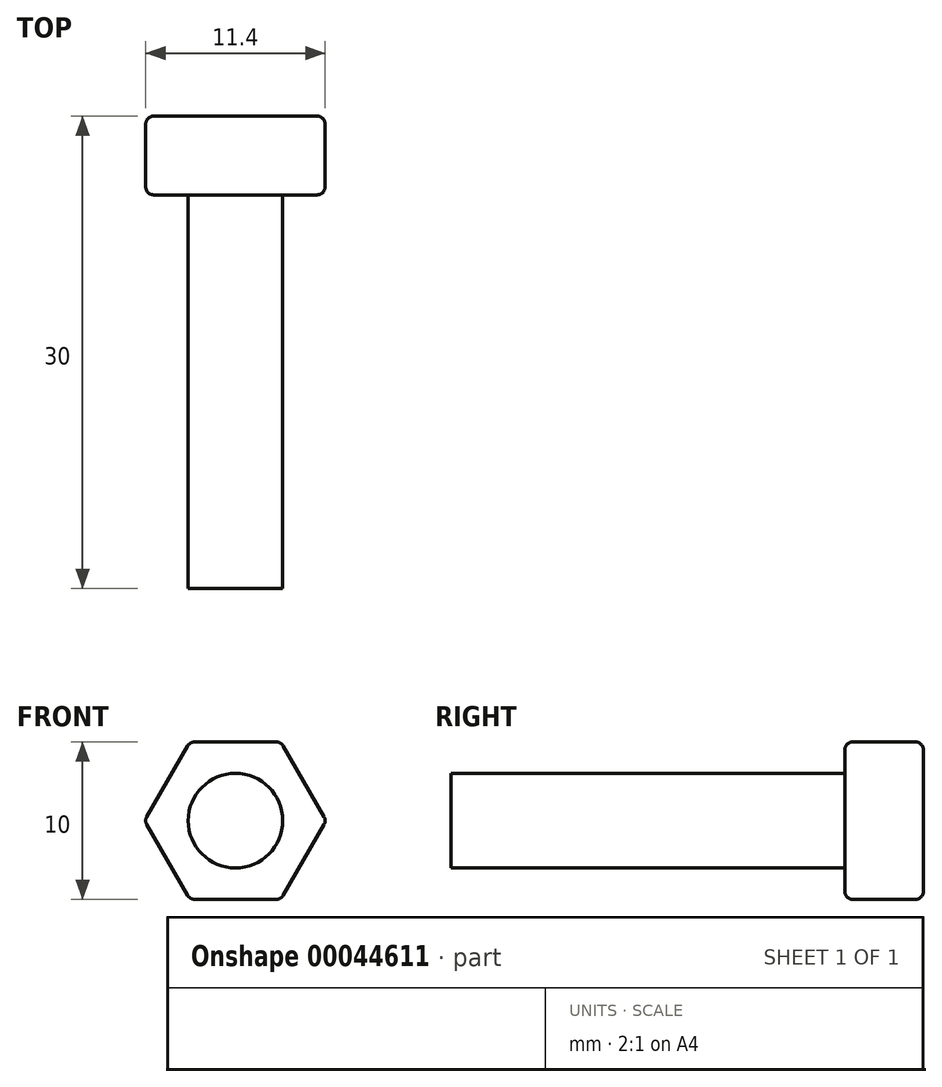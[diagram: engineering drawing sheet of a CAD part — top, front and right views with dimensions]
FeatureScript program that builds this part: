
annotation { "Feature Type Name" : "Feature", "Feature Type Description" : "" }
export const myFeature = defineFeature(function(context is Context, id is Id, definition is map)
    precondition{}
    {
        {
            var Q0;
            Q0=qCreatedBy(makeId("Front.planeOp"),FACE);
            var sketch = newSketch(context, id + "F0", { "sketchPlane" : qUnion([Q0])});
            skCircle(sketch, "E0", {"center": v(0, 0) * mm, "radius": 3 * mm});
            skCircle(sketch, "E1", {"center": v(0, 0) * mm, "radius": 5 * mm, "construction": true});
            skLineSegment(sketch, "E2.0", {"start": v(2.89, -5) * mm, "end": v(-2.89, -5) * mm});
            skLineSegment(sketch, "E2.1", {"start": v(-2.89, -5) * mm, "end": v(-5.77, 0) * mm});
            skLineSegment(sketch, "E2.2", {"start": v(-5.77, 0) * mm, "end": v(-2.89, 5) * mm});
            skLineSegment(sketch, "E2.3", {"start": v(-2.89, 5) * mm, "end": v(2.89, 5) * mm});
            skLineSegment(sketch, "E2.4", {"start": v(2.89, 5) * mm, "end": v(5.77, 0) * mm});
            skLineSegment(sketch, "E2.5", {"start": v(5.77, 0) * mm, "end": v(2.89, -5) * mm});
            skPoint(sketch, "E2.0.midPoint", {"position": v(0, -5) * mm});
            skSolve(sketch);
        }
        {
            var Q0;
            Q0=makeQuery(id+"F0.imprint","IMPRINT",FACE,{"disambiguationData":[TD([[makeQuery(id+"F0.imprint","IMPRINT",EDGE,{"derivedFrom":sQuery(id+"F0.wireOp",EDGE,"E0")}),1.0]])]});
            extrude(context, id + "F1", {"entities" : qUnion([Q0]), "depth" : 25 * mm});
        }
        {
            var Q0;
            Q0=makeQuery(id+"F0.imprint","IMPRINT",FACE,{"disambiguationData":[TD([[makeQuery(id+"F0.imprint","IMPRINT",EDGE,{"derivedFrom":sQuery(id+"F0.wireOp",EDGE,"E0")}),-1.0]])]});
            var Q1;
            Q1=makeQuery(id+"F0.imprint","IMPRINT",FACE,{"disambiguationData":[TD([[makeQuery(id+"F0.imprint","IMPRINT",EDGE,{"derivedFrom":sQuery(id+"F0.wireOp",EDGE,"E0")}),1.0]])]});
            extrude(context, id + "F2", {"entities" : qUnion([Q0, Q1]), "operationType" : NewBodyOperationType.ADD, "oppositeDirection" : true, "depth" : 5 * mm});
        }
        {
            var Q0;
            Q0=makeQuery(id+"F2.opExtrude","SWEPT_FACE",FACE,{"disambiguationData":[OSD([sQuery(id+"F0.wireOp",EDGE,"E2.0")])]});
            var Q1;
            Q1=makeQuery(id+"F2.opExtrude","SWEPT_FACE",FACE,{"disambiguationData":[OSD([sQuery(id+"F0.wireOp",EDGE,"E2.5")])]});
            var Q2;
            Q2=makeQuery(id+"F2.opExtrude","CAP_FACE",FACE,{"disambiguationData":[OSD([sQuery(id+"F0.wireOp",EDGE,"E2.0"),sQuery(id+"F0.wireOp",EDGE,"E2.1"),sQuery(id+"F0.wireOp",EDGE,"E2.2"),sQuery(id+"F0.wireOp",EDGE,"E2.3"),sQuery(id+"F0.wireOp",EDGE,"E2.4"),sQuery(id+"F0.wireOp",EDGE,"E2.5")])],"isStart":false});
            var Q3;
            Q3=makeQuery(id+"F2.opExtrude","SWEPT_FACE",FACE,{"disambiguationData":[OSD([sQuery(id+"F0.wireOp",EDGE,"E2.1")])]});
            var Q4;
            Q4=makeQuery(id+"F2.opExtrude","SWEPT_FACE",FACE,{"disambiguationData":[OSD([sQuery(id+"F0.wireOp",EDGE,"E2.2")])]});
            var Q5;
            Q5=makeQuery(id+"F2.opExtrude","SWEPT_FACE",FACE,{"disambiguationData":[OSD([sQuery(id+"F0.wireOp",EDGE,"E2.3")])]});
            var Q6;
            Q6=makeQuery(id+"F2.opExtrude","SWEPT_FACE",FACE,{"disambiguationData":[OSD([sQuery(id+"F0.wireOp",EDGE,"E2.4")])]});
            fillet(context, id + "F3", {"entities" : qUnion([Q0, Q1, Q2, Q3, Q4, Q5, Q6]), "radius" : 0.5 * mm, "tangentPropagation" : true, "allowEdgeOverflow" : false});
        }
    });
